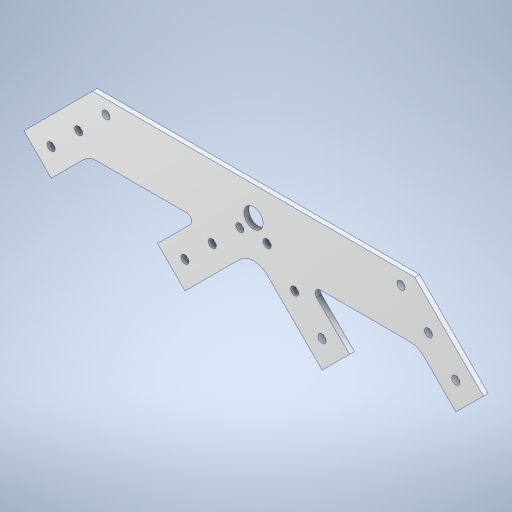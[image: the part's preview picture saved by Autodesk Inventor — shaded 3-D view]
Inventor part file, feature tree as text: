
AUTODESK INVENTOR PART (.ipt)
format: ipt  version: 2023 (Build 270158000, 158)  size: 360,960 bytes
history: native  units: in
note: dims shown in document units (in); Inventor stores cm internally (conversion verified against a paired STEP export)
features: extrude x2, fillet x2, sketch x2, projected_geometry x2, other x1, mirror x1
ambient origin geometry x8: Origin, YZ Plane, XZ Plane, XY Plane, X Axis, Y Axis, Z Axis, Center Point
bodies: Solid1 (feature_tree)
feature tree (10):
  other  "<userpath>\OneDrive\Desktop\Robotics\URC Chassis Pivot\PivotParametersAndCalcs.xlsx"
  extrude  "Extrusion1"  Depth=2.5in
  extrude  "Extrusion3"  Depth=0.125in TaperAngle=0.0deg
  mirror  "Mirror2"
  fillet  "Fillet1"  Radius=1.0in
  fillet  "Fillet2"  Radius=1.0in
  sketch  "Sketch4"  dims[d6=45.0deg d7=0.125in d8=0.0in d15=1.0in d59=1.0in d61=4.0in d62=1.5in d63=0.75in d64=0.2087in d65=1.1811in d67=1.0in d68=0.3937in d70=1.0in d72=0.5in d73=0.5in d74=1.1811in d76=1.0in d77=0.3937in d79=1.0in d81=1.0in d82=0.0in d83=0.75in d84=0.5in d85=0.125in d86=2.0in d87=4.5962in]
  sketch  "Sketch3"  dims[d1=0.5in d4=2.5in]
  projected_geometry  "Projected Loop2"
  projected_geometry  "Projected Loop3"
